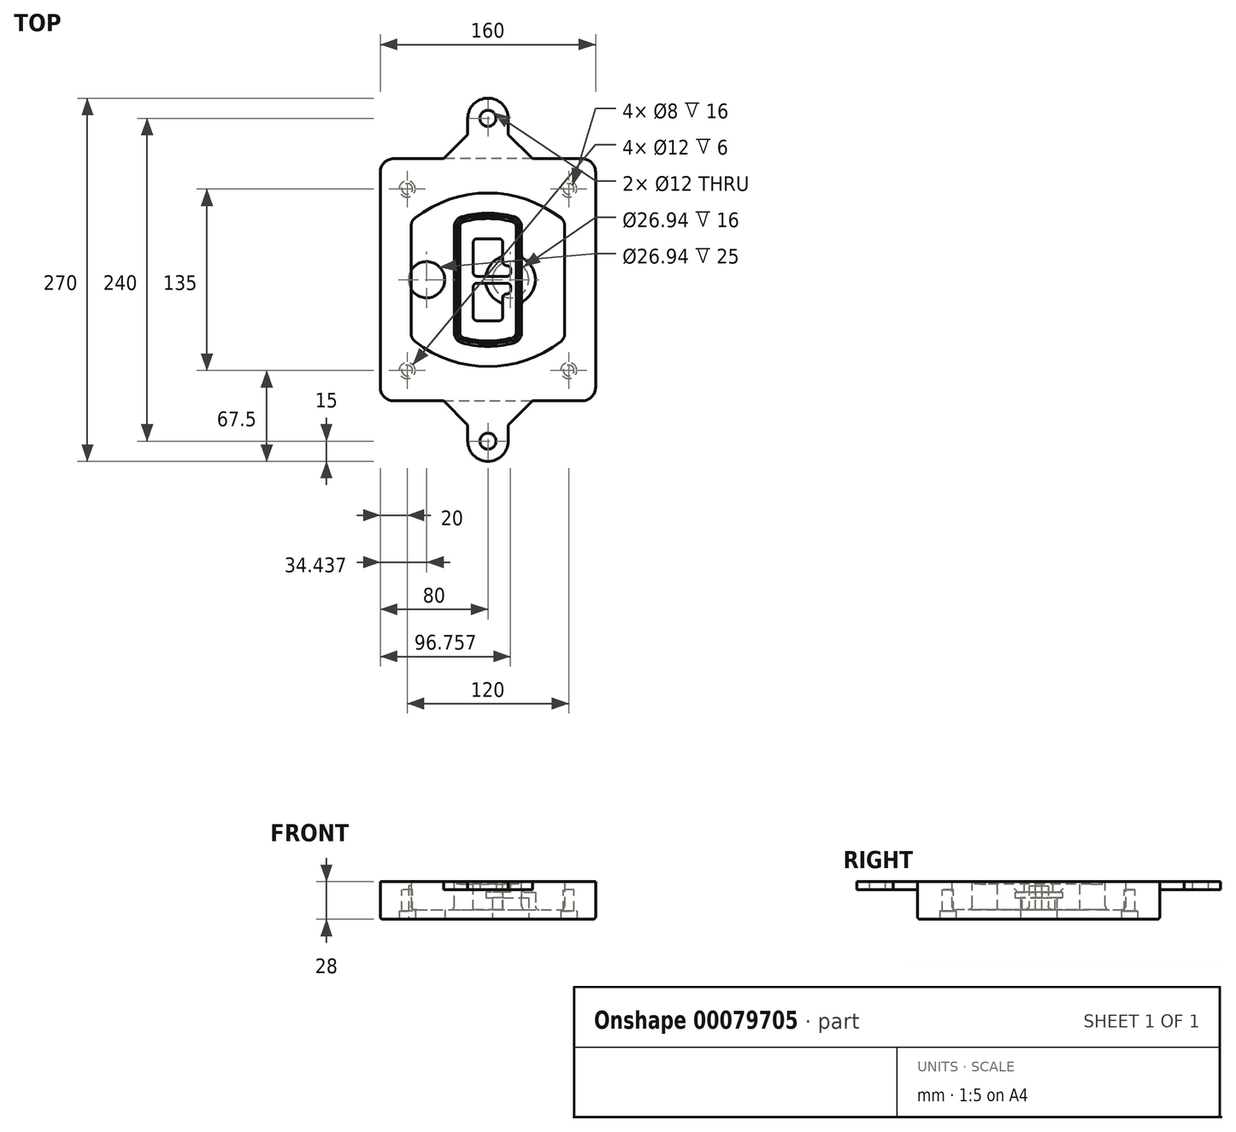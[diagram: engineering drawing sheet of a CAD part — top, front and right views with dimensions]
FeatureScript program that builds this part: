
annotation { "Feature Type Name" : "Feature", "Feature Type Description" : "" }
export const myFeature = defineFeature(function(context is Context, id is Id, definition is map)
    precondition{}
    {
        {
            var Q0;
            Q0=qCreatedBy(makeId("Top.planeOp"),FACE);
            var sketch = newSketch(context, id + "F0", { "sketchPlane" : qUnion([Q0])});
            skPoint(sketch, "E0.rect.middle", {"position": v(0, 0) * mm});
            skLineSegment(sketch, "E1.bottom", {"start": v(-70, -90) * mm, "end": v(70, -90) * mm});
            skLineSegment(sketch, "E1.top", {"start": v(-70, 90) * mm, "end": v(70, 90) * mm});
            skLineSegment(sketch, "E1.left", {"start": v(-80, -80) * mm, "end": v(-80, 80) * mm});
            skLineSegment(sketch, "E1.right", {"start": v(80, -80) * mm, "end": v(80, 80) * mm});
            skLineSegment(sketch, "E2", {"start": v(-80, 90) * mm, "end": v(80, -90) * mm, "construction": true});
            skLineSegment(sketch, "E3", {"start": v(80, 90) * mm, "end": v(-80, -90) * mm, "construction": true});
            skCircle(sketch, "E4", {"center": v(-60, 67.5) * mm, "radius": 4 * mm});
            skCircle(sketch, "E5", {"center": v(60, 67.5) * mm, "radius": 4 * mm});
            skCircle(sketch, "E6", {"center": v(60, -67.5) * mm, "radius": 4 * mm});
            skCircle(sketch, "E7", {"center": v(-60, -67.5) * mm, "radius": 4 * mm});
            skLineSegment(sketch, "E8", {"start": v(-60, 67.5) * mm, "end": v(60, 67.5) * mm, "construction": true});
            skLineSegment(sketch, "E9", {"start": v(60, 67.5) * mm, "end": v(60, -67.5) * mm, "construction": true});
            skLineSegment(sketch, "E10", {"start": v(60, -67.5) * mm, "end": v(-60, -67.5) * mm, "construction": true});
            skLineSegment(sketch, "E11", {"start": v(-60, -67.5) * mm, "end": v(-60, 67.5) * mm, "construction": true});
            skLineSegment(sketch, "E12", {"start": v(-60, 40.3) * mm, "end": v(-60, -40.3) * mm});
            skLineSegment(sketch, "E13", {"start": v(60, 40.3) * mm, "end": v(60, -40.3) * mm});
            skArc(sketch, "E14", {"start": v(56.15, 48.18) * mm, "mid": v(0, 67.5) * mm, "end": v(-56.15, 48.18) * mm});
            skArc(sketch, "E15", {"start": v(-56.15, -48.18) * mm, "mid": v(0, -67.5) * mm, "end": v(56.15, -48.18) * mm});
            skLineSegment(sketch, "E16", {"start": v(-60, 0) * mm, "end": v(60, 0) * mm, "construction": true});
            skPoint(sketch, "E17.visualSharp", {"position": v(-60, -45) * mm});
            skArc(sketch, "E17.filletArc", {"start": v(-60, -40.3) * mm, "mid": v(-58.99, -44.68) * mm, "end": v(-56.15, -48.18) * mm});
            skPoint(sketch, "E18.visualSharp", {"position": v(-60, 45) * mm});
            skArc(sketch, "E18.filletArc", {"start": v(-56.15, 48.18) * mm, "mid": v(-58.99, 44.68) * mm, "end": v(-60, 40.3) * mm});
            skPoint(sketch, "E19.visualSharp", {"position": v(60, 45) * mm});
            skArc(sketch, "E19.filletArc", {"start": v(60, 40.3) * mm, "mid": v(58.99, 44.68) * mm, "end": v(56.15, 48.18) * mm});
            skPoint(sketch, "E20.visualSharp", {"position": v(60, -45) * mm});
            skArc(sketch, "E20.filletArc", {"start": v(56.15, -48.18) * mm, "mid": v(58.99, -44.68) * mm, "end": v(60, -40.3) * mm});
            skPoint(sketch, "E21.visualSharp", {"position": v(-80, 90) * mm});
            skArc(sketch, "E21.filletArc", {"start": v(-70, 90) * mm, "mid": v(-77.07, 87.07) * mm, "end": v(-80, 80) * mm});
            skPoint(sketch, "E22.visualSharp", {"position": v(80, 90) * mm});
            skArc(sketch, "E22.filletArc", {"start": v(80, 80) * mm, "mid": v(77.07, 87.07) * mm, "end": v(70, 90) * mm});
            skPoint(sketch, "E23.visualSharp", {"position": v(80, -90) * mm});
            skArc(sketch, "E23.filletArc", {"start": v(70, -90) * mm, "mid": v(77.07, -87.07) * mm, "end": v(80, -80) * mm});
            skPoint(sketch, "E24.visualSharp", {"position": v(-80, -90) * mm});
            skArc(sketch, "E24.filletArc", {"start": v(-80, -80) * mm, "mid": v(-77.07, -87.07) * mm, "end": v(-70, -90) * mm});
            skArc(sketch, "E25.0", {"start": v(57, 40.3) * mm, "mid": v(56.3, 43.36) * mm, "end": v(54.3, 45.81) * mm});
            skLineSegment(sketch, "E25.1", {"start": v(57, 40.3) * mm, "end": v(57, -40.3) * mm});
            skArc(sketch, "E25.2", {"start": v(54.3, -45.81) * mm, "mid": v(56.3, -43.36) * mm, "end": v(57, -40.3) * mm});
            skArc(sketch, "E25.3", {"start": v(-54.3, -45.81) * mm, "mid": v(0, -64.5) * mm, "end": v(54.3, -45.81) * mm});
            skArc(sketch, "E25.4", {"start": v(-57, -40.3) * mm, "mid": v(-56.3, -43.36) * mm, "end": v(-54.3, -45.81) * mm});
            skArc(sketch, "E25.5", {"start": v(54.3, 45.81) * mm, "mid": v(0, 64.5) * mm, "end": v(-54.3, 45.81) * mm});
            skLineSegment(sketch, "E25.6", {"start": v(-57, 40.3) * mm, "end": v(-57, -40.3) * mm});
            skArc(sketch, "E25.7", {"start": v(-54.3, 45.81) * mm, "mid": v(-56.3, 43.36) * mm, "end": v(-57, 40.3) * mm});
            skArc(sketch, "E26.0", {"start": v(-58.62, 51.33) * mm, "mid": v(-62.58, 46.43) * mm, "end": v(-64, 40.3) * mm});
            skArc(sketch, "E26.1", {"start": v(58.62, 51.33) * mm, "mid": v(0, 71.5) * mm, "end": v(-58.62, 51.33) * mm});
            skArc(sketch, "E26.2", {"start": v(64, 40.3) * mm, "mid": v(62.58, 46.43) * mm, "end": v(58.62, 51.33) * mm});
            skLineSegment(sketch, "E26.3", {"start": v(64, 40.3) * mm, "end": v(64, -40.3) * mm});
            skArc(sketch, "E26.4", {"start": v(58.62, -51.33) * mm, "mid": v(62.58, -46.43) * mm, "end": v(64, -40.3) * mm});
            skLineSegment(sketch, "E26.5", {"start": v(-64, 40.3) * mm, "end": v(-64, -40.3) * mm});
            skArc(sketch, "E26.6", {"start": v(-58.62, -51.33) * mm, "mid": v(0, -71.5) * mm, "end": v(58.62, -51.33) * mm});
            skArc(sketch, "E26.7", {"start": v(-64, -40.3) * mm, "mid": v(-62.58, -46.43) * mm, "end": v(-58.62, -51.33) * mm});
            skSolve(sketch);
        }
        {
            var Q0;
            Q0=makeQuery(id+"F0.imprint","IMPRINT",FACE,{"disambiguationData":[TD([[makeQuery(id+"F0.imprint","IMPRINT",EDGE,{"derivedFrom":sQuery(id+"F0.wireOp",EDGE,"E1.bottom")}),1.0]])]});
            var Q1;
            Q1=makeQuery(id+"F0.imprint","IMPRINT",FACE,{"disambiguationData":[TD([[makeQuery(id+"F0.imprint","IMPRINT",EDGE,{"derivedFrom":sQuery(id+"F0.wireOp",EDGE,"E12")}),1.0]])]});
            var Q2;
            Q2=makeQuery(id+"F0.imprint","IMPRINT",FACE,{"disambiguationData":[TD([[makeQuery(id+"F0.imprint","IMPRINT",EDGE,{"derivedFrom":sQuery(id+"F0.wireOp",EDGE,"E25.0")}),1.0]])]});
            var Q3;
            Q3=makeQuery(id+"F0.imprint","IMPRINT",FACE,{"disambiguationData":[TD([[makeQuery(id+"F0.imprint","IMPRINT",EDGE,{"derivedFrom":sQuery(id+"F0.wireOp",EDGE,"E12")}),-1.0]])]});
            extrude(context, id + "F1", {"entities" : qUnion([Q0, Q1, Q2, Q3]), "oppositeDirection" : true, "depth" : 25 * mm});
        }
        {
            var Q0;
            Q0=makeQuery(id+"F0.imprint","IMPRINT",FACE,{"disambiguationData":[TD([[makeQuery(id+"F0.imprint","IMPRINT",EDGE,{"derivedFrom":sQuery(id+"F0.wireOp",EDGE,"E12")}),1.0]])]});
            extrude(context, id + "F2", {"entities" : qUnion([Q0]), "operationType" : NewBodyOperationType.ADD, "depth" : 3 * mm});
        }
        {
            var Q0;
            Q0=makeQuery(id+"F0.imprint","IMPRINT",FACE,{"disambiguationData":[TD([[makeQuery(id+"F0.imprint","IMPRINT",EDGE,{"derivedFrom":sQuery(id+"F0.wireOp",EDGE,"E25.0")}),1.0]])]});
            extrude(context, id + "F3", {"entities" : qUnion([Q0]), "operationType" : NewBodyOperationType.REMOVE, "oppositeDirection" : true, "depth" : 18 * mm});
        }
        {
            var Q0;
            Q0=makeQuery(id+"F2.opExtrude","CAP_FACE",FACE,{"disambiguationData":[OSD([sQuery(id+"F0.wireOp",EDGE,"E12"),sQuery(id+"F0.wireOp",EDGE,"E13"),sQuery(id+"F0.wireOp",EDGE,"E14"),sQuery(id+"F0.wireOp",EDGE,"E15"),sQuery(id+"F0.wireOp",EDGE,"E17.filletArc"),sQuery(id+"F0.wireOp",EDGE,"E18.filletArc"),sQuery(id+"F0.wireOp",EDGE,"E19.filletArc"),sQuery(id+"F0.wireOp",EDGE,"E20.filletArc"),sQuery(id+"F0.wireOp",EDGE,"E25.0"),sQuery(id+"F0.wireOp",EDGE,"E25.1"),sQuery(id+"F0.wireOp",EDGE,"E25.2"),sQuery(id+"F0.wireOp",EDGE,"E25.3"),sQuery(id+"F0.wireOp",EDGE,"E25.4"),sQuery(id+"F0.wireOp",EDGE,"E25.5"),sQuery(id+"F0.wireOp",EDGE,"E25.6"),sQuery(id+"F0.wireOp",EDGE,"E25.7")])],"isStart":false});
            var sketch = newSketch(context, id + "F4", { "sketchPlane" : qUnion([Q0])});
            skArc(sketch, "E27.0", {"start": v(-19.08, -46.97) * mm, "mid": v(0, -49.5) * mm, "end": v(19.08, -46.97) * mm});
            skArc(sketch, "E28.0", {"start": v(19.08, 46.97) * mm, "mid": v(0, 49.5) * mm, "end": v(-19.08, 46.97) * mm});
            skLineSegment(sketch, "E29", {"start": v(-25, 39.25) * mm, "end": v(-25, -39.25) * mm});
            skLineSegment(sketch, "E30", {"start": v(25, 39.25) * mm, "end": v(25, -39.25) * mm});
            skLineSegment(sketch, "E31", {"start": v(-25, 45.1) * mm, "end": v(25, 45.1) * mm, "construction": true});
            skLineSegment(sketch, "E32", {"start": v(-25, -45.1) * mm, "end": v(25, -45.1) * mm, "construction": true});
            skPoint(sketch, "E33.visualSharp", {"position": v(-25, 45.1) * mm});
            skArc(sketch, "E33.filletArc", {"start": v(-19.08, 46.97) * mm, "mid": v(-23.35, 44.11) * mm, "end": v(-25, 39.25) * mm});
            skPoint(sketch, "E34.visualSharp", {"position": v(25, 45.1) * mm});
            skArc(sketch, "E34.filletArc", {"start": v(25, 39.25) * mm, "mid": v(23.35, 44.11) * mm, "end": v(19.08, 46.97) * mm});
            skPoint(sketch, "E35.visualSharp", {"position": v(25, -45.1) * mm});
            skArc(sketch, "E35.filletArc", {"start": v(19.08, -46.97) * mm, "mid": v(23.35, -44.11) * mm, "end": v(25, -39.25) * mm});
            skPoint(sketch, "E36.visualSharp", {"position": v(-25, -45.1) * mm});
            skArc(sketch, "E36.filletArc", {"start": v(-25, -39.25) * mm, "mid": v(-23.35, -44.11) * mm, "end": v(-19.08, -46.97) * mm});
            skArc(sketch, "E37.0", {"start": v(54.3, 45.81) * mm, "mid": v(0, 64.5) * mm, "end": v(-54.3, 45.81) * mm});
            skArc(sketch, "E37.1", {"start": v(-54.3, 45.81) * mm, "mid": v(-56.3, 43.36) * mm, "end": v(-57, 40.3) * mm});
            skLineSegment(sketch, "E37.2", {"start": v(-57, 40.3) * mm, "end": v(-57, -40.3) * mm});
            skArc(sketch, "E37.3", {"start": v(-57, -40.3) * mm, "mid": v(-56.3, -43.36) * mm, "end": v(-54.3, -45.81) * mm});
            skArc(sketch, "E37.4", {"start": v(-54.3, -45.81) * mm, "mid": v(0, -64.5) * mm, "end": v(54.3, -45.81) * mm});
            skArc(sketch, "E37.5", {"start": v(54.3, -45.81) * mm, "mid": v(56.3, -43.36) * mm, "end": v(57, -40.3) * mm});
            skLineSegment(sketch, "E37.6", {"start": v(57, 40.3) * mm, "end": v(57, -40.3) * mm});
            skArc(sketch, "E37.7", {"start": v(57, 40.3) * mm, "mid": v(56.3, 43.36) * mm, "end": v(54.3, 45.81) * mm});
            skLineSegment(sketch, "E38.0", {"start": v(23, 39.25) * mm, "end": v(23, -39.25) * mm});
            skArc(sketch, "E38.1", {"start": v(18.56, -45.04) * mm, "mid": v(21.76, -42.9) * mm, "end": v(23, -39.25) * mm});
            skArc(sketch, "E38.2", {"start": v(-18.56, -45.04) * mm, "mid": v(0, -47.5) * mm, "end": v(18.56, -45.04) * mm});
            skArc(sketch, "E38.3", {"start": v(-23, -39.25) * mm, "mid": v(-21.76, -42.9) * mm, "end": v(-18.56, -45.04) * mm});
            skLineSegment(sketch, "E38.4", {"start": v(-23, 39.25) * mm, "end": v(-23, -39.25) * mm});
            skArc(sketch, "E38.5", {"start": v(23, 39.25) * mm, "mid": v(21.76, 42.9) * mm, "end": v(18.56, 45.04) * mm});
            skArc(sketch, "E38.6", {"start": v(-18.56, 45.04) * mm, "mid": v(-21.76, 42.9) * mm, "end": v(-23, 39.25) * mm});
            skArc(sketch, "E38.7", {"start": v(18.56, 45.04) * mm, "mid": v(0, 47.5) * mm, "end": v(-18.56, 45.04) * mm});
            skArc(sketch, "E39.0", {"start": v(21, 39.25) * mm, "mid": v(20.18, 41.68) * mm, "end": v(18.04, 43.1) * mm});
            skLineSegment(sketch, "E39.1", {"start": v(21, 39.25) * mm, "end": v(21, -39.25) * mm});
            skArc(sketch, "E39.2", {"start": v(18.04, -43.1) * mm, "mid": v(20.18, -41.68) * mm, "end": v(21, -39.25) * mm});
            skArc(sketch, "E39.3", {"start": v(-18.04, -43.1) * mm, "mid": v(0, -45.5) * mm, "end": v(18.04, -43.1) * mm});
            skArc(sketch, "E39.4", {"start": v(-21, -39.25) * mm, "mid": v(-20.18, -41.68) * mm, "end": v(-18.04, -43.1) * mm});
            skArc(sketch, "E39.5", {"start": v(18.04, 43.1) * mm, "mid": v(0, 45.5) * mm, "end": v(-18.04, 43.1) * mm});
            skLineSegment(sketch, "E39.6", {"start": v(-21, 39.25) * mm, "end": v(-21, -39.25) * mm});
            skArc(sketch, "E39.7", {"start": v(-18.04, 43.1) * mm, "mid": v(-20.18, 41.68) * mm, "end": v(-21, 39.25) * mm});
            skLineSegment(sketch, "E40", {"start": v(-25, 0) * mm, "end": v(25, 0) * mm, "construction": true});
            skLineSegment(sketch, "E41", {"start": v(-11, 5.5) * mm, "end": v(-11, 27.5) * mm});
            skLineSegment(sketch, "E42", {"start": v(-8, 30.5) * mm, "end": v(8, 30.5) * mm});
            skLineSegment(sketch, "E43", {"start": v(11, 27.5) * mm, "end": v(11, 13.5) * mm});
            skLineSegment(sketch, "E44", {"start": v(14, 10.5) * mm, "end": v(14, 10.5) * mm});
            skLineSegment(sketch, "E45", {"start": v(17, 7.5) * mm, "end": v(17, 5.5) * mm});
            skLineSegment(sketch, "E46", {"start": v(14, 2.5) * mm, "end": v(-8, 2.5) * mm});
            skPoint(sketch, "E47.visualSharp", {"position": v(-11, 30.5) * mm});
            skArc(sketch, "E47.filletArc", {"start": v(-8, 30.5) * mm, "mid": v(-10.12, 29.62) * mm, "end": v(-11, 27.5) * mm});
            skPoint(sketch, "E48.visualSharp", {"position": v(11, 30.5) * mm});
            skArc(sketch, "E48.filletArc", {"start": v(11, 27.5) * mm, "mid": v(10.12, 29.62) * mm, "end": v(8, 30.5) * mm});
            skPoint(sketch, "E49.visualSharp", {"position": v(11, 10.5) * mm});
            skArc(sketch, "E49.filletArc", {"start": v(11, 13.5) * mm, "mid": v(11.88, 11.38) * mm, "end": v(14, 10.5) * mm});
            skPoint(sketch, "E50.visualSharp", {"position": v(17, 10.5) * mm});
            skArc(sketch, "E50.filletArc", {"start": v(17, 7.5) * mm, "mid": v(16.12, 9.62) * mm, "end": v(14, 10.5) * mm});
            skPoint(sketch, "E51.visualSharp", {"position": v(17, 2.5) * mm});
            skArc(sketch, "E51.filletArc", {"start": v(14, 2.5) * mm, "mid": v(16.12, 3.38) * mm, "end": v(17, 5.5) * mm});
            skPoint(sketch, "E52.visualSharp", {"position": v(-11, 2.5) * mm});
            skArc(sketch, "E52.filletArc", {"start": v(-11, 5.5) * mm, "mid": v(-10.12, 3.38) * mm, "end": v(-8, 2.5) * mm});
            skLineSegment(sketch, "E53.0.MirrorCS", {"start": v(14, -2.5) * mm, "end": v(-8, -2.5) * mm});
            skArc(sketch, "E54.0.MirrorCS", {"start": v(-11, -5.5) * mm, "mid": v(-10.12, -3.38) * mm, "end": v(-8, -2.5) * mm});
            skLineSegment(sketch, "E55.0.MirrorCS", {"start": v(-11, -5.5) * mm, "end": v(-11, -27.5) * mm});
            skArc(sketch, "E56.0.MirrorCS", {"start": v(-8, -30.5) * mm, "mid": v(-10.12, -29.62) * mm, "end": v(-11, -27.5) * mm});
            skLineSegment(sketch, "E57.0.MirrorCS", {"start": v(-8, -30.5) * mm, "end": v(8, -30.5) * mm});
            skArc(sketch, "E58.0.MirrorCS", {"start": v(11, -27.5) * mm, "mid": v(10.12, -29.62) * mm, "end": v(8, -30.5) * mm});
            skLineSegment(sketch, "E59.0.MirrorCS", {"start": v(11, -27.5) * mm, "end": v(11, -13.5) * mm});
            skArc(sketch, "E60.0.MirrorCS", {"start": v(11, -13.5) * mm, "mid": v(11.88, -11.38) * mm, "end": v(14, -10.5) * mm});
            skArc(sketch, "E61.0.MirrorCS", {"start": v(17, -7.5) * mm, "mid": v(16.12, -9.62) * mm, "end": v(14, -10.5) * mm});
            skLineSegment(sketch, "E62.0.MirrorCS", {"start": v(17, -7.5) * mm, "end": v(17, -5.5) * mm});
            skArc(sketch, "E63.0.MirrorCS", {"start": v(14, -2.5) * mm, "mid": v(16.12, -3.38) * mm, "end": v(17, -5.5) * mm});
            skSolve(sketch);
        }
        {
            var Q0;
            Q0=makeQuery(id+"F4.imprint","IMPRINT",FACE,{"disambiguationData":[TD([[makeQuery(id+"F4.imprint","IMPRINT",EDGE,{"derivedFrom":sQuery(id+"F4.wireOp",EDGE,"E27.0")}),1.0]])]});
            var Q1;
            Q1=makeQuery(id+"F4.imprint","IMPRINT",FACE,{"disambiguationData":[TD([[makeQuery(id+"F4.imprint","IMPRINT",EDGE,{"derivedFrom":sQuery(id+"F4.wireOp",EDGE,"E38.0")}),-1.0]])]});
            var Q2;
            Q2=makeQuery(id+"F4.imprint","IMPRINT",FACE,{"disambiguationData":[TD([[makeQuery(id+"F4.imprint","IMPRINT",EDGE,{"derivedFrom":sQuery(id+"F4.wireOp",EDGE,"E39.0")}),1.0]])]});
            extrude(context, id + "F5", {"entities" : qUnion([Q0, Q1, Q2]), "operationType" : NewBodyOperationType.ADD, "endBound" : BoundingType.UP_TO_NEXT, "oppositeDirection" : true, "depth" : 25 * mm});
        }
        {
            var Q0;
            Q0=makeQuery(id+"F4.imprint","IMPRINT",FACE,{"disambiguationData":[TD([[makeQuery(id+"F4.imprint","IMPRINT",EDGE,{"derivedFrom":sQuery(id+"F4.wireOp",EDGE,"E38.0")}),-1.0]])]});
            extrude(context, id + "F6", {"entities" : qUnion([Q0]), "operationType" : NewBodyOperationType.REMOVE, "oppositeDirection" : true, "depth" : 2 * mm});
        }
        {
            var Q0;
            Q0=makeQuery(id+"F1.opExtrude","CAP_FACE",FACE,{"disambiguationData":[OSD([sQuery(id+"F0.wireOp",EDGE,"E1.bottom"),sQuery(id+"F0.wireOp",EDGE,"E1.top"),sQuery(id+"F0.wireOp",EDGE,"E1.left"),sQuery(id+"F0.wireOp",EDGE,"E1.right"),sQuery(id+"F0.wireOp",EDGE,"E4"),sQuery(id+"F0.wireOp",EDGE,"E5"),sQuery(id+"F0.wireOp",EDGE,"E6"),sQuery(id+"F0.wireOp",EDGE,"E7"),sQuery(id+"F0.wireOp",EDGE,"E21.filletArc"),sQuery(id+"F0.wireOp",EDGE,"E22.filletArc"),sQuery(id+"F0.wireOp",EDGE,"E23.filletArc"),sQuery(id+"F0.wireOp",EDGE,"E24.filletArc")])],"isStart":false});
            var sketch = newSketch(context, id + "F7", { "sketchPlane" : qUnion([Q0])});
            skCircle(sketch, "E64", {"center": v(16.76, 0) * mm, "radius": 13.47 * mm});
            skCircle(sketch, "E65", {"center": v(-45.56, 0) * mm, "radius": 13.47 * mm});
            skLineSegment(sketch, "E66", {"start": v(80, 0) * mm, "end": v(-80, 0) * mm});
            skCircle(sketch, "E67", {"center": v(16.76, 0) * mm, "radius": 18.47 * mm});
            skCircle(sketch, "E68", {"center": v(60, -67.5) * mm, "radius": 6 * mm});
            skCircle(sketch, "E69", {"center": v(-60, -67.5) * mm, "radius": 6 * mm});
            skCircle(sketch, "E70", {"center": v(-60, 67.5) * mm, "radius": 6 * mm});
            skCircle(sketch, "E71", {"center": v(60, 67.5) * mm, "radius": 6 * mm});
            skSolve(sketch);
        }
        {
            var Q0;
            {var subQ1=sQuery(id+"F7.wireOp",EDGE,"E66");var subQ4=sQuery(id+"F7.wireOp",EDGE,"E64");var subQ6=makeQuery(id+"F7.imprint","INTERSECT",VERTEX,{"disambiguationData":[OD(0.0)],"derivedFrom":[subQ4,subQ1]});Q0=makeQuery(id+"F7.imprint","IMPRINT",FACE,{"disambiguationData":[TD([[makeQuery(id+"F7.imprint","IMPRINT",EDGE,{"disambiguationData":[TD([[subQ6,-1.0]])],"derivedFrom":subQ4}),-1.0]])]});}
            var Q1;
            {var subQ0=sQuery(id+"F7.wireOp",EDGE,"E66");var subQ1=sQuery(id+"F7.wireOp",EDGE,"E64");var subQ3=makeQuery(id+"F7.imprint","INTERSECT",VERTEX,{"disambiguationData":[OD(0.0)],"derivedFrom":[subQ1,subQ0]});Q1=makeQuery(id+"F7.imprint","IMPRINT",FACE,{"disambiguationData":[TD([[makeQuery(id+"F7.imprint","IMPRINT",EDGE,{"disambiguationData":[TD([[subQ3,-1.0]])],"derivedFrom":subQ1}),1.0]])]});}
            var Q2;
            {var subQ0=sQuery(id+"F7.wireOp",EDGE,"E66");var subQ1=sQuery(id+"F7.wireOp",EDGE,"E64");var subQ3=makeQuery(id+"F7.imprint","INTERSECT",VERTEX,{"disambiguationData":[OD(0.0)],"derivedFrom":[subQ1,subQ0]});Q2=makeQuery(id+"F7.imprint","IMPRINT",FACE,{"disambiguationData":[TD([[makeQuery(id+"F7.imprint","IMPRINT",EDGE,{"disambiguationData":[TD([[subQ3,1.0]])],"derivedFrom":subQ1}),1.0]])]});}
            var Q3;
            {var subQ1=sQuery(id+"F7.wireOp",EDGE,"E66");var subQ4=sQuery(id+"F7.wireOp",EDGE,"E64");var subQ6=makeQuery(id+"F7.imprint","INTERSECT",VERTEX,{"disambiguationData":[OD(0.0)],"derivedFrom":[subQ4,subQ1]});Q3=makeQuery(id+"F7.imprint","IMPRINT",FACE,{"disambiguationData":[TD([[makeQuery(id+"F7.imprint","IMPRINT",EDGE,{"disambiguationData":[TD([[subQ6,1.0]])],"derivedFrom":subQ4}),-1.0]])]});}
            extrude(context, id + "F8", {"entities" : qUnion([Q0, Q1, Q2, Q3]), "operationType" : NewBodyOperationType.ADD, "oppositeDirection" : true, "depth" : 20 * mm});
        }
        {
            var Q0;
            {var subQ0=sQuery(id+"F7.wireOp",EDGE,"E66");var subQ1=sQuery(id+"F7.wireOp",EDGE,"E64");var subQ3=makeQuery(id+"F7.imprint","INTERSECT",VERTEX,{"disambiguationData":[OD(0.0)],"derivedFrom":[subQ1,subQ0]});Q0=makeQuery(id+"F7.imprint","IMPRINT",FACE,{"disambiguationData":[TD([[makeQuery(id+"F7.imprint","IMPRINT",EDGE,{"disambiguationData":[TD([[subQ3,-1.0]])],"derivedFrom":subQ1}),1.0]])]});}
            var Q1;
            {var subQ0=sQuery(id+"F7.wireOp",EDGE,"E66");var subQ1=sQuery(id+"F7.wireOp",EDGE,"E64");var subQ3=makeQuery(id+"F7.imprint","INTERSECT",VERTEX,{"disambiguationData":[OD(0.0)],"derivedFrom":[subQ1,subQ0]});Q1=makeQuery(id+"F7.imprint","IMPRINT",FACE,{"disambiguationData":[TD([[makeQuery(id+"F7.imprint","IMPRINT",EDGE,{"disambiguationData":[TD([[subQ3,1.0]])],"derivedFrom":subQ1}),1.0]])]});}
            extrude(context, id + "F9", {"entities" : qUnion([Q0, Q1]), "operationType" : NewBodyOperationType.REMOVE, "oppositeDirection" : true, "depth" : 16 * mm});
        }
        {
            var Q0;
            {var subQ0=sQuery(id+"F7.wireOp",EDGE,"E66");var subQ1=sQuery(id+"F7.wireOp",EDGE,"E65");var subQ3=makeQuery(id+"F7.imprint","INTERSECT",VERTEX,{"disambiguationData":[OD(0.0)],"derivedFrom":[subQ1,subQ0]});Q0=makeQuery(id+"F7.imprint","IMPRINT",FACE,{"disambiguationData":[TD([[makeQuery(id+"F7.imprint","IMPRINT",EDGE,{"disambiguationData":[TD([[subQ3,-1.0]])],"derivedFrom":subQ1}),1.0]])]});}
            var Q1;
            {var subQ0=sQuery(id+"F7.wireOp",EDGE,"E66");var subQ1=sQuery(id+"F7.wireOp",EDGE,"E65");var subQ3=makeQuery(id+"F7.imprint","INTERSECT",VERTEX,{"disambiguationData":[OD(0.0)],"derivedFrom":[subQ1,subQ0]});Q1=makeQuery(id+"F7.imprint","IMPRINT",FACE,{"disambiguationData":[TD([[makeQuery(id+"F7.imprint","IMPRINT",EDGE,{"disambiguationData":[TD([[subQ3,1.0]])],"derivedFrom":subQ1}),1.0]])]});}
            extrude(context, id + "F10", {"entities" : qUnion([Q0, Q1]), "operationType" : NewBodyOperationType.REMOVE, "oppositeDirection" : true, "depth" : 25 * mm});
        }
        {
            var Q0;
            Q0=makeQuery(id+"F7.imprint","IMPRINT",FACE,{"disambiguationData":[TD([[makeQuery(id+"F7.imprint","IMPRINT",EDGE,{"derivedFrom":sQuery(id+"F7.wireOp",EDGE,"E68")}),1.0]])]});
            var Q1;
            Q1=makeQuery(id+"F7.imprint","IMPRINT",FACE,{"disambiguationData":[TD([[makeQuery(id+"F7.imprint","IMPRINT",EDGE,{"derivedFrom":makeQuery(id+"F1.opExtrude","CAP_EDGE",EDGE,{"disambiguationData":[OSD([sQuery(id+"F0.wireOp",EDGE,"E5")])],"isStart":false})}),-1.0]])]});
            var Q2;
            Q2=makeQuery(id+"F7.imprint","IMPRINT",FACE,{"disambiguationData":[TD([[makeQuery(id+"F7.imprint","IMPRINT",EDGE,{"derivedFrom":sQuery(id+"F7.wireOp",EDGE,"E69")}),1.0]])]});
            var Q3;
            Q3=makeQuery(id+"F7.imprint","IMPRINT",FACE,{"disambiguationData":[TD([[makeQuery(id+"F7.imprint","IMPRINT",EDGE,{"derivedFrom":makeQuery(id+"F1.opExtrude","CAP_EDGE",EDGE,{"disambiguationData":[OSD([sQuery(id+"F0.wireOp",EDGE,"E4")])],"isStart":false})}),-1.0]])]});
            var Q4;
            Q4=makeQuery(id+"F7.imprint","IMPRINT",FACE,{"disambiguationData":[TD([[makeQuery(id+"F7.imprint","IMPRINT",EDGE,{"derivedFrom":sQuery(id+"F7.wireOp",EDGE,"E70")}),1.0]])]});
            var Q5;
            Q5=makeQuery(id+"F7.imprint","IMPRINT",FACE,{"disambiguationData":[TD([[makeQuery(id+"F7.imprint","IMPRINT",EDGE,{"derivedFrom":makeQuery(id+"F1.opExtrude","CAP_EDGE",EDGE,{"disambiguationData":[OSD([sQuery(id+"F0.wireOp",EDGE,"E7")])],"isStart":false})}),-1.0]])]});
            var Q6;
            Q6=makeQuery(id+"F7.imprint","IMPRINT",FACE,{"disambiguationData":[TD([[makeQuery(id+"F7.imprint","IMPRINT",EDGE,{"derivedFrom":sQuery(id+"F7.wireOp",EDGE,"E71")}),1.0]])]});
            var Q7;
            Q7=makeQuery(id+"F7.imprint","IMPRINT",FACE,{"disambiguationData":[TD([[makeQuery(id+"F7.imprint","IMPRINT",EDGE,{"derivedFrom":makeQuery(id+"F1.opExtrude","CAP_EDGE",EDGE,{"disambiguationData":[OSD([sQuery(id+"F0.wireOp",EDGE,"E6")])],"isStart":false})}),-1.0]])]});
            extrude(context, id + "F11", {"entities" : qUnion([Q0, Q1, Q2, Q3, Q4, Q5, Q6, Q7]), "operationType" : NewBodyOperationType.REMOVE, "oppositeDirection" : true, "depth" : 6 * mm});
        }
        {
            var Q0;
            Q0=makeQuery(id+"F9.boolean.opBoolean","COPY",FACE,{"derivedFrom":makeQuery(id+"F9.opExtrude","CAP_FACE",FACE,{"disambiguationData":[OSD([sQuery(id+"F7.wireOp",EDGE,"E64")])],"isStart":false})});
            var sketch = newSketch(context, id + "F12", { "sketchPlane" : qUnion([Q0])});
            skArc(sketch, "E72.0", {"start": v(11, 17.55) * mm, "mid": v(2.57, 11.82) * mm, "end": v(-1.54, 2.5) * mm});
            skArc(sketch, "E72.1", {"start": v(-1.54, -2.5) * mm, "mid": v(2.57, -11.82) * mm, "end": v(11, -17.55) * mm});
            skLineSegment(sketch, "E73", {"start": v(-1.54, -2.5) * mm, "end": v(14, -2.5) * mm});
            skLineSegment(sketch, "E74.0", {"start": v(14, 2.5) * mm, "end": v(-1.54, 2.5) * mm});
            skArc(sketch, "E74.1", {"start": v(14, 2.5) * mm, "mid": v(16.12, 3.38) * mm, "end": v(17, 5.5) * mm});
            skLineSegment(sketch, "E74.2", {"start": v(17, 7.5) * mm, "end": v(17, 5.5) * mm});
            skArc(sketch, "E74.3", {"start": v(17, 7.5) * mm, "mid": v(16.12, 9.62) * mm, "end": v(14, 10.5) * mm});
            skArc(sketch, "E74.4", {"start": v(11, 13.5) * mm, "mid": v(11.88, 11.38) * mm, "end": v(14, 10.5) * mm});
            skLineSegment(sketch, "E74.5", {"start": v(11, 17.55) * mm, "end": v(11, 13.5) * mm});
            skLineSegment(sketch, "E74.7", {"start": v(14, -2.5) * mm, "end": v(-1.54, -2.5) * mm});
            skArc(sketch, "E74.8", {"start": v(14, -2.5) * mm, "mid": v(16.12, -3.38) * mm, "end": v(17, -5.5) * mm});
            skLineSegment(sketch, "E74.9", {"start": v(17, -7.5) * mm, "end": v(17, -5.5) * mm});
            skArc(sketch, "E74.10", {"start": v(17, -7.5) * mm, "mid": v(16.12, -9.62) * mm, "end": v(14, -10.5) * mm});
            skArc(sketch, "E74.11", {"start": v(11, -13.5) * mm, "mid": v(11.88, -11.38) * mm, "end": v(14, -10.5) * mm});
            skLineSegment(sketch, "E74.12", {"start": v(11, -17.55) * mm, "end": v(11, -13.5) * mm});
            skPoint(sketch, "E75.orphan", {"position": v(11, -27.5) * mm});
            skPoint(sketch, "E76.orphan", {"position": v(-8, -2.5) * mm});
            skPoint(sketch, "E77.orphan", {"position": v(-8, 2.5) * mm});
            skPoint(sketch, "E78.orphan", {"position": v(11, 27.5) * mm});
            skSolve(sketch);
        }
        {
            var Q0;
            {var subQ7=sQuery(id+"F12.wireOp",EDGE,"E72.0");var subQ14=sQuery(id+"F12.wireOp",EDGE,"E72.1");var subQ16=sQuery(id+"F12.wireOp",EDGE,"E74.1");var subQ18=sQuery(id+"F12.wireOp",EDGE,"E74.8");Q0=qUnion([makeQuery(id+"F12.imprint","IMPRINT",FACE,{"disambiguationData":[TD([[makeQuery(id+"F12.imprint","IMPRINT",EDGE,{"derivedFrom":subQ7}),1.0]])]}),makeQuery(id+"F12.imprint","IMPRINT",FACE,{"disambiguationData":[TD([[makeQuery(id+"F12.imprint","IMPRINT",EDGE,{"derivedFrom":subQ14}),1.0]])]}),makeQuery(id+"F12.imprint","IMPRINT",FACE,{"disambiguationData":[TD([[makeQuery(id+"F12.imprint","IMPRINT",EDGE,{"derivedFrom":subQ16}),1.0]])]}),makeQuery(id+"F12.imprint","IMPRINT",FACE,{"disambiguationData":[TD([[makeQuery(id+"F12.imprint","IMPRINT",EDGE,{"derivedFrom":subQ18}),-1.0]])]})]);}
            var Q1;
            Q1=makeQuery(id+"F5.boolean.opBoolean","SPLIT",FACE,{"disambiguationData":[TD([makeQuery(id+"F5.opExtrude","SWEPT_FACE",FACE,{"disambiguationData":[OSD([sQuery(id+"F4.wireOp",EDGE,"E41")])]})])],"derivedFrom":makeQuery(id+"F3.boolean.opBoolean","COPY",FACE,{"derivedFrom":makeQuery(id+"F3.opExtrude","CAP_FACE",FACE,{"disambiguationData":[OSD([sQuery(id+"F0.wireOp",EDGE,"E25.0"),sQuery(id+"F0.wireOp",EDGE,"E25.1"),sQuery(id+"F0.wireOp",EDGE,"E25.2"),sQuery(id+"F0.wireOp",EDGE,"E25.3"),sQuery(id+"F0.wireOp",EDGE,"E25.4"),sQuery(id+"F0.wireOp",EDGE,"E25.5"),sQuery(id+"F0.wireOp",EDGE,"E25.6"),sQuery(id+"F0.wireOp",EDGE,"E25.7")])],"isStart":false})})});
            extrude(context, id + "F13", {"entities" : qUnion([Q0]), "operationType" : NewBodyOperationType.REMOVE, "endBound" : BoundingType.UP_TO_SURFACE, "endBoundEntityFace" : qUnion([Q1]), "depth" : 25 * mm});
        }
        {
            var Q0;
            Q0=makeQuery(id+"F3.boolean.opBoolean","COPY",EDGE,{"derivedFrom":makeQuery(id+"F3.opExtrude","CAP_EDGE",EDGE,{"disambiguationData":[OSD([sQuery(id+"F0.wireOp",EDGE,"E25.6")])],"isStart":false})});
            var Q1;
            Q1=makeQuery(id+"F8.boolean.opBoolean","INTERSECT",EDGE,{"derivedFrom":[makeQuery(id+"F5.opExtrude","SWEPT_FACE",FACE,{"disambiguationData":[OSD([sQuery(id+"F4.wireOp",EDGE,"E30")])]}),makeQuery(id+"F8.opExtrude","CAP_FACE",FACE,{"disambiguationData":[OSD([sQuery(id+"F7.wireOp",EDGE,"E67")])],"isStart":false})]});
            var Q2;
            Q2=makeQuery(id+"F8.boolean.opBoolean","INTERSECT",EDGE,{"disambiguationData":[OD(1.0)],"derivedFrom":[makeQuery(id+"F5.opExtrude","SWEPT_FACE",FACE,{"disambiguationData":[OSD([sQuery(id+"F4.wireOp",EDGE,"E30")])]}),makeQuery(id+"F8.opExtrude","SWEPT_FACE",FACE,{"disambiguationData":[OSD([sQuery(id+"F7.wireOp",EDGE,"E67")])]})]});
            var Q3;
            {var subQ0=sQuery(id+"F4.wireOp",EDGE,"E30");Q3=makeQuery(id+"F8.boolean.opBoolean","SPLIT",EDGE,{"disambiguationData":[TD([makeQuery(id+"F5.opExtrude","SWEPT_FACE",FACE,{"disambiguationData":[OSD([sQuery(id+"F4.wireOp",EDGE,"E35.filletArc")])]})])],"derivedFrom":makeQuery(id+"F5.opExtrude","CAP_EDGE",EDGE,{"disambiguationData":[OSD([subQ0])],"isStart":false})});}
            var Q4;
            {var subQ0=sQuery(id+"F0.wireOp",EDGE,"E25.7");var subQ1=sQuery(id+"F0.wireOp",EDGE,"E25.1");var subQ2=sQuery(id+"F0.wireOp",EDGE,"E25.6");var subQ3=sQuery(id+"F0.wireOp",EDGE,"E25.5");var subQ4=sQuery(id+"F0.wireOp",EDGE,"E25.4");var subQ5=sQuery(id+"F0.wireOp",EDGE,"E25.0");var subQ6=sQuery(id+"F0.wireOp",EDGE,"E25.2");var subQ7=sQuery(id+"F0.wireOp",EDGE,"E25.3");Q4=makeQuery(id+"F8.boolean.opBoolean","INTERSECT",EDGE,{"derivedFrom":[makeQuery(id+"F5.boolean.opBoolean","SPLIT",FACE,{"disambiguationData":[TD([makeQuery(id+"F2.opExtrude","SWEPT_FACE",FACE,{"disambiguationData":[OSD([subQ5])]})])],"derivedFrom":makeQuery(id+"F3.boolean.opBoolean","COPY",FACE,{"derivedFrom":makeQuery(id+"F3.opExtrude","CAP_FACE",FACE,{"disambiguationData":[OSD([subQ5,subQ1,subQ6,subQ7,subQ4,subQ3,subQ2,subQ0])],"isStart":false})})}),makeQuery(id+"F8.opExtrude","SWEPT_FACE",FACE,{"disambiguationData":[OSD([sQuery(id+"F7.wireOp",EDGE,"E67")])]})]});}
            var Q5;
            Q5=makeQuery(id+"F8.boolean.opBoolean","INTERSECT",EDGE,{"disambiguationData":[OD(0.0)],"derivedFrom":[makeQuery(id+"F5.opExtrude","SWEPT_FACE",FACE,{"disambiguationData":[OSD([sQuery(id+"F4.wireOp",EDGE,"E30")])]}),makeQuery(id+"F8.opExtrude","SWEPT_FACE",FACE,{"disambiguationData":[OSD([sQuery(id+"F7.wireOp",EDGE,"E67")])]})]});
            fillet(context, id + "F14", {"entities" : qUnion([Q0, Q1, Q2, Q3, Q4, Q5]), "radius" : 3 * mm, "tangentPropagation" : true, "allowEdgeOverflow" : false});
        }
        {
            var Q0;
            Q0=makeQuery(id+"F1.opExtrude","CAP_EDGE",EDGE,{"disambiguationData":[OSD([sQuery(id+"F0.wireOp",EDGE,"E1.bottom")])],"isStart":false});
            fillet(context, id + "F15", {"entities" : qUnion([Q0]), "radius" : 2 * mm, "tangentPropagation" : true, "allowEdgeOverflow" : false});
        }
        {
            var Q0;
            {var subQ0=sQuery(id+"F0.wireOp",EDGE,"E22.filletArc");var subQ1=sQuery(id+"F0.wireOp",EDGE,"E7");var subQ2=sQuery(id+"F0.wireOp",EDGE,"E6");var subQ3=sQuery(id+"F0.wireOp",EDGE,"E5");var subQ4=sQuery(id+"F0.wireOp",EDGE,"E4");var subQ5=sQuery(id+"F0.wireOp",EDGE,"E1.bottom");var subQ6=sQuery(id+"F0.wireOp",EDGE,"E21.filletArc");var subQ7=sQuery(id+"F0.wireOp",EDGE,"E1.top");var subQ8=sQuery(id+"F0.wireOp",EDGE,"E1.left");var subQ9=sQuery(id+"F0.wireOp",EDGE,"E1.right");var subQ10=sQuery(id+"F0.wireOp",EDGE,"E23.filletArc");var subQ11=sQuery(id+"F0.wireOp",EDGE,"E24.filletArc");Q0=makeQuery(id+"F2.boolean.opBoolean","SPLIT",FACE,{"disambiguationData":[TD([makeQuery(id+"F1.opExtrude","SWEPT_FACE",FACE,{"disambiguationData":[OSD([subQ5])]})])],"derivedFrom":makeQuery(id+"F1.opExtrude","CAP_FACE",FACE,{"disambiguationData":[OSD([subQ5,subQ7,subQ8,subQ9,subQ4,subQ3,subQ2,subQ1,subQ6,subQ0,subQ10,subQ11])],"isStart":true})});}
            var sketch = newSketch(context, id + "F16", { "sketchPlane" : qUnion([Q0])});
            skLineSegment(sketch, "E79", {"start": v(0, 90) * mm, "end": v(0, 120) * mm, "construction": true});
            skCircle(sketch, "E80", {"center": v(0, 120) * mm, "radius": 6 * mm});
            skLineSegment(sketch, "E81", {"start": v(15, 120) * mm, "end": v(15, 108) * mm});
            skLineSegment(sketch, "E82", {"start": v(15, 108) * mm, "end": v(33, 90) * mm});
            skLineSegment(sketch, "E83", {"start": v(-15, 120) * mm, "end": v(-15, 108) * mm});
            skLineSegment(sketch, "E84", {"start": v(-15, 108) * mm, "end": v(-33, 90) * mm});
            skArc(sketch, "E85", {"start": v(15, 120) * mm, "mid": v(0, 135) * mm, "end": v(-15, 120) * mm});
            skLineSegment(sketch, "E86", {"start": v(-80, 0) * mm, "end": v(80, 0) * mm, "construction": true});
            skCircle(sketch, "E87.MirrorC", {"center": v(0, -120) * mm, "radius": 6 * mm});
            skLineSegment(sketch, "E88.MirrorCS", {"start": v(0, -90) * mm, "end": v(0, -120) * mm, "construction": true});
            skLineSegment(sketch, "E89.MirrorCS", {"start": v(-15, -120) * mm, "end": v(-15, -108) * mm});
            skLineSegment(sketch, "E90.MirrorCS", {"start": v(-15, -108) * mm, "end": v(-33, -90) * mm});
            skLineSegment(sketch, "E91.MirrorCS", {"start": v(15, -108) * mm, "end": v(33, -90) * mm});
            skArc(sketch, "E92.MirrorCS", {"start": v(15, -120) * mm, "mid": v(0, -135) * mm, "end": v(-15, -120) * mm});
            skLineSegment(sketch, "E93.MirrorCS", {"start": v(15, -120) * mm, "end": v(15, -108) * mm});
            skLineSegment(sketch, "E94.0", {"start": v(-80, -80) * mm, "end": v(-80, 80) * mm});
            skArc(sketch, "E94.1", {"start": v(-80, -80) * mm, "mid": v(-77.07, -87.07) * mm, "end": v(-70, -90) * mm});
            skLineSegment(sketch, "E94.2", {"start": v(-70, -90) * mm, "end": v(70, -90) * mm});
            skArc(sketch, "E94.3", {"start": v(70, -90) * mm, "mid": v(77.07, -87.07) * mm, "end": v(80, -80) * mm});
            skLineSegment(sketch, "E94.4", {"start": v(80, -80) * mm, "end": v(80, 80) * mm});
            skArc(sketch, "E94.5", {"start": v(80, 80) * mm, "mid": v(77.07, 87.07) * mm, "end": v(70, 90) * mm});
            skLineSegment(sketch, "E94.6", {"start": v(-70, 90) * mm, "end": v(70, 90) * mm});
            skArc(sketch, "E94.7", {"start": v(-70, 90) * mm, "mid": v(-77.07, 87.07) * mm, "end": v(-80, 80) * mm});
            skArc(sketch, "E94.8", {"start": v(56.15, 48.18) * mm, "mid": v(0, 67.5) * mm, "end": v(-56.15, 48.18) * mm});
            skArc(sketch, "E94.9", {"start": v(-56.15, 48.18) * mm, "mid": v(-58.99, 44.68) * mm, "end": v(-60, 40.3) * mm});
            skLineSegment(sketch, "E94.10", {"start": v(-60, 40.3) * mm, "end": v(-60, -40.3) * mm});
            skArc(sketch, "E94.11", {"start": v(-60, -40.3) * mm, "mid": v(-58.99, -44.68) * mm, "end": v(-56.15, -48.18) * mm});
            skArc(sketch, "E94.12", {"start": v(-56.15, -48.18) * mm, "mid": v(0, -67.5) * mm, "end": v(56.15, -48.18) * mm});
            skArc(sketch, "E94.13", {"start": v(56.15, -48.18) * mm, "mid": v(58.99, -44.68) * mm, "end": v(60, -40.3) * mm});
            skLineSegment(sketch, "E94.14", {"start": v(60, 40.3) * mm, "end": v(60, -40.3) * mm});
            skPoint(sketch, "E94.15", {"position": v(60, 40.3) * mm});
            skArc(sketch, "E94.16", {"start": v(60, 40.3) * mm, "mid": v(58.99, 44.68) * mm, "end": v(56.15, 48.18) * mm});
            skSolve(sketch);
        }
        {
            var Q0;
            Q0 = qSketchRegion(id + "F16", true);
            extrude(context, id + "F17", {"entities" : qUnion([Q0]), "operationType" : NewBodyOperationType.ADD, "endBound" : BoundingType.SYMMETRIC, "depth" : 6 * mm});
        }
    });
